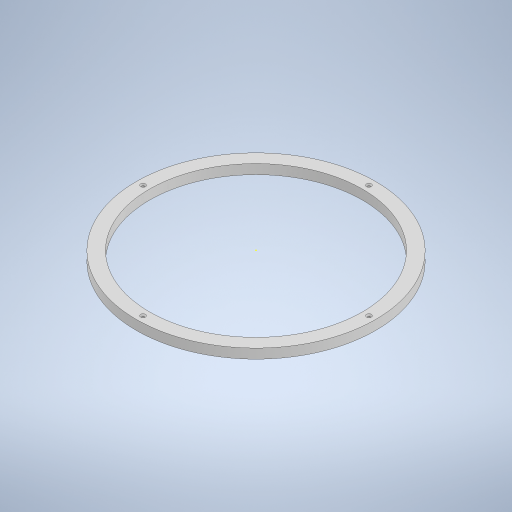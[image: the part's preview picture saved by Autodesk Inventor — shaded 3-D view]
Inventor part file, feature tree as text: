
AUTODESK INVENTOR PART (.ipt)
format: ipt  version: 2023 (Build 270158000, 158)  size: 261,120 bytes
history: native  units: in
note: dims shown in document units (in); Inventor stores cm internally (conversion verified against a paired STEP export)
features: sketch x3, extrude x1, hole x1, pattern_circular x1
ambient origin geometry x8: Origin, YZ Plane, XZ Plane, XY Plane, X Axis, Y Axis, Z Axis, Center Point
bodies: Solid1 (feature_tree)
feature tree (6):
  extrude  "Extrusion1"  Depth=8.7598in
  hole  "Hole1"  [1 undecoded]
  pattern_circular  "Circular Pattern1"  Count=4 Angle=360.0deg
  sketch  "Sketch3"  dims[d6=0.0984in d7=0.2362in d8=0.1969in d9=0.0787in d10=90.0deg d11=0.315in d12=0.8108in d13=1.5748in d14=360.0deg]
  sketch  "Sketch1"  dims[d0=9.8425in d1=8.7598in]
  sketch  "Sketch2"  dims[d2=0.3937in d3=0.0in d4=9.3012in]
note: 1 required parameter value undecoded (feature->parameter linkage not recoverable at this tier; creation-order binding heuristic only, values carry confidence <= 0.55)
